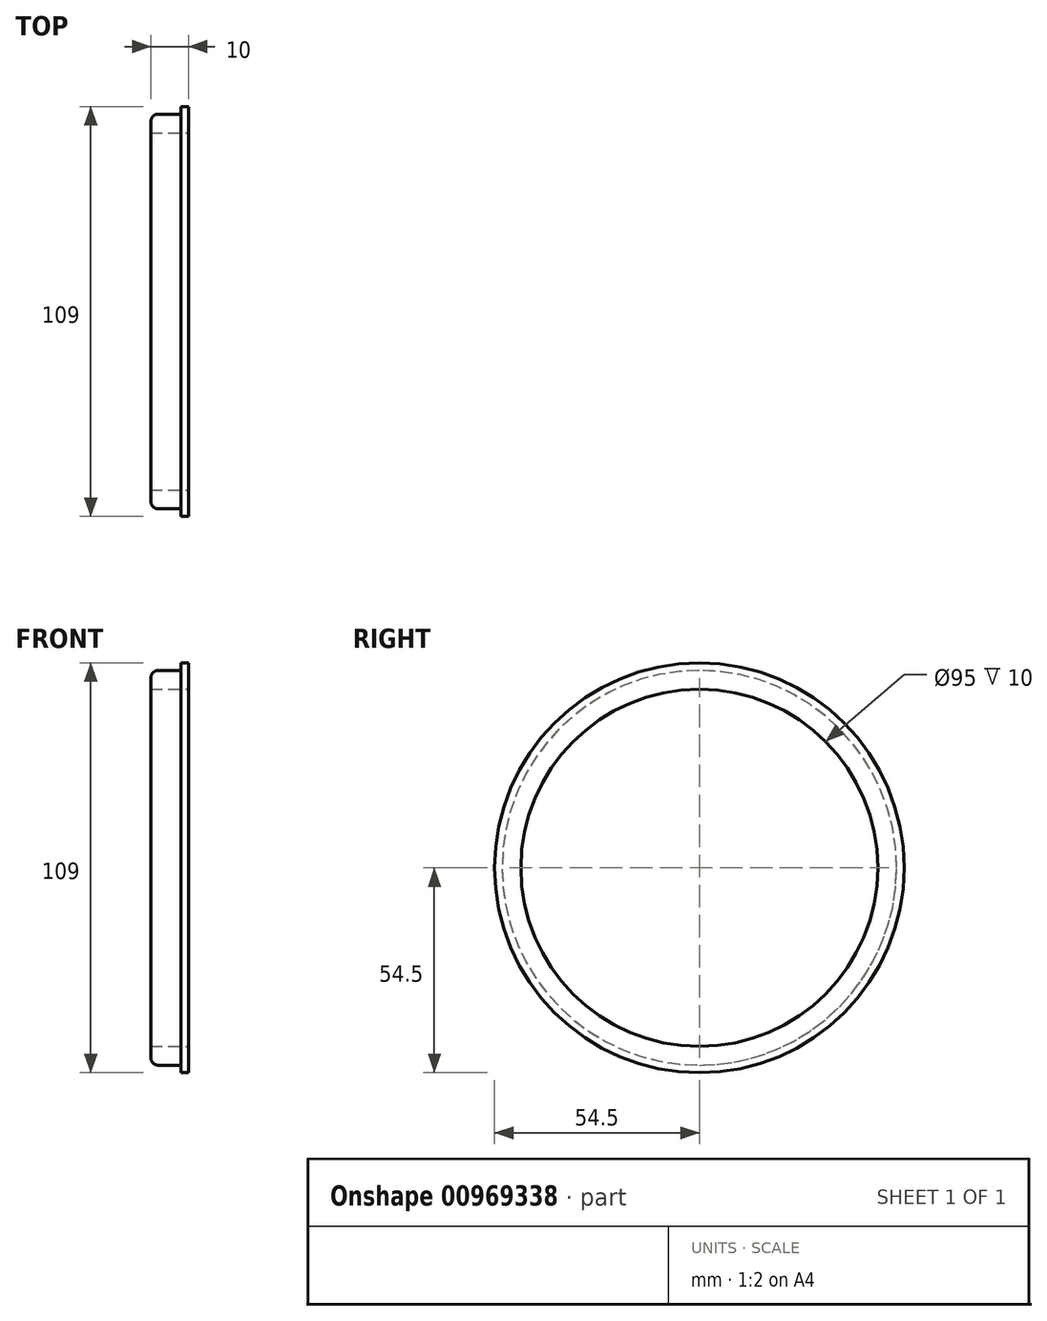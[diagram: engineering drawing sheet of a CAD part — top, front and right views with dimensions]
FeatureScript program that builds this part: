
annotation { "Feature Type Name" : "Feature", "Feature Type Description" : "" }
export const myFeature = defineFeature(function(context is Context, id is Id, definition is map)
    precondition{}
    {
        {
            var Q0;
            Q0=qCreatedBy(makeId("Front.planeOp"),FACE);
            var sketch = newSketch(context, id + "F0", { "sketchPlane" : qUnion([Q0])});
            skLineSegment(sketch, "E0", {"start": v(0, 0) * mm, "end": v(-98.32, 0) * mm, "construction": true});
            skLineSegment(sketch, "E1", {"start": v(0, 47.5) * mm, "end": v(0, 54.5) * mm});
            skLineSegment(sketch, "E2", {"start": v(0, 54.5) * mm, "end": v(-2, 54.5) * mm});
            skLineSegment(sketch, "E3", {"start": v(-2, 54.5) * mm, "end": v(-2, 52.5) * mm});
            skLineSegment(sketch, "E4", {"start": v(-2, 52.5) * mm, "end": v(-10, 52.5) * mm});
            skLineSegment(sketch, "E5", {"start": v(-10, 52.5) * mm, "end": v(-10, 47.5) * mm});
            skLineSegment(sketch, "E6", {"start": v(-10, 47.5) * mm, "end": v(0, 47.5) * mm});
            skSolve(sketch);
        }
        {
            var Q0;
            Q0=makeQuery(id+"F0.imprint","IMPRINT",FACE,{"disambiguationData":[TD([[makeQuery(id+"F0.imprint","IMPRINT",EDGE,{"derivedFrom":sQuery(id+"F0.wireOp",EDGE,"E1")}),1.0]])]});
            var Q1;
            Q1=sQuery(id+"F0.wireOp",EDGE,"E0");
            revolve(context, id + "F1", {"surfaceOperationType" : NewSurfaceOperationType.NEW, "entities" : qUnion([Q0]), "axis" : qUnion([Q1]), "revolveType" : RevolveType.FULL});
        }
        {
            var Q0;
            Q0=makeQuery(id+"F1.opRevolve","SWEPT_EDGE",EDGE,{"disambiguationData":[OSD([sQuery(id+"F0.wireOp",EDGE,"E4"),sQuery(id+"F0.wireOp",EDGE,"E5")])]});
            fillet(context, id + "F2", {"entities" : qUnion([Q0]), "radius" : 1.93 * mm, "tangentPropagation" : true, "allowEdgeOverflow" : false});
        }
    });
